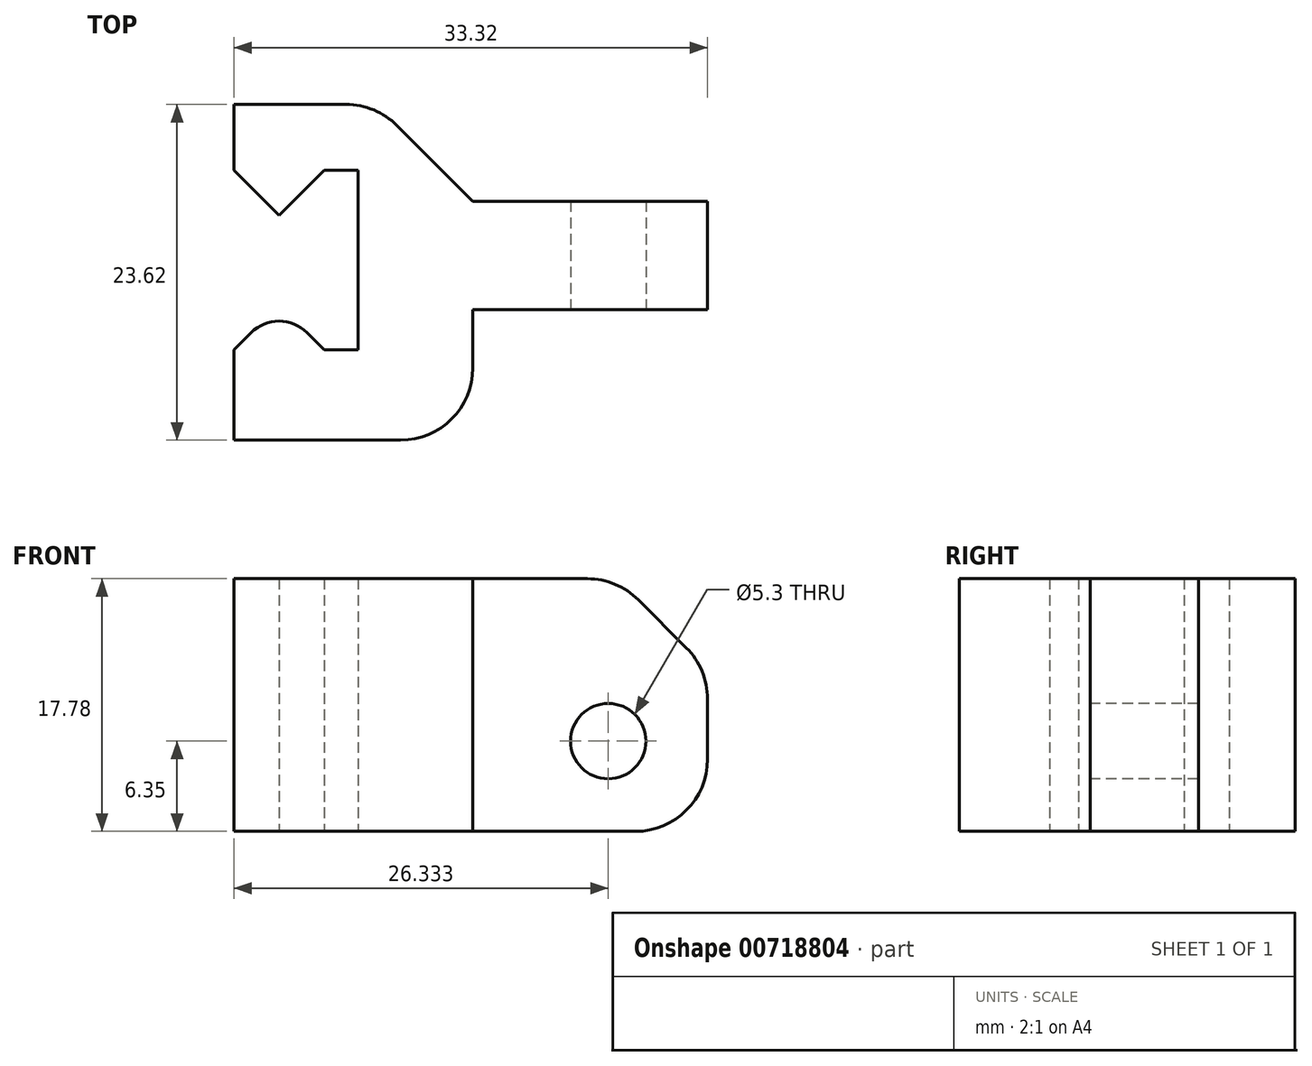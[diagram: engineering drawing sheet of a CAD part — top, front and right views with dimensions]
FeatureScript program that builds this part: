
annotation { "Feature Type Name" : "Feature", "Feature Type Description" : "" }
export const myFeature = defineFeature(function(context is Context, id is Id, definition is map)
    precondition{}
    {
        {
            var Q0;
            Q0=qCreatedBy(makeId("Top.planeOp"),FACE);
            var sketch = newSketch(context, id + "F0", { "sketchPlane" : qUnion([Q0])});
            skLineSegment(sketch, "E0", {"start": v(5.56, -11.6) * mm, "end": v(3.18, -11.6) * mm});
            skLineSegment(sketch, "E1", {"start": v(3.18, -11.6) * mm, "end": v(0, -8.43) * mm});
            skLineSegment(sketch, "E2", {"start": v(0, -8.43) * mm, "end": v(-3.18, -11.6) * mm});
            skLineSegment(sketch, "E3", {"start": v(-3.18, -11.6) * mm, "end": v(-3.18, -17.96) * mm});
            skLineSegment(sketch, "E4", {"start": v(-3.18, -17.96) * mm, "end": v(30.44, -17.96) * mm});
            skLineSegment(sketch, "E5", {"start": v(-0.4, 5.66) * mm, "end": v(6.81, 5.66) * mm});
            skLineSegment(sketch, "E6", {"start": v(6.81, 5.66) * mm, "end": v(30.44, -17.96) * mm});
            skPoint(sketch, "E7.endSnap0", {"position": v(13.63, -17.96) * mm});
            skLineSegment(sketch, "E8", {"start": v(13.63, -1.15) * mm, "end": v(13.63, -17.96) * mm});
            skLineSegment(sketch, "E9", {"start": v(5.56, -11.6) * mm, "end": v(5.56, 1.03) * mm});
            skLineSegment(sketch, "E10", {"start": v(3.18, 1.03) * mm, "end": v(5.56, 1.03) * mm});
            skLineSegment(sketch, "E11", {"start": v(3.18, 1.03) * mm, "end": v(0, -2.15) * mm});
            skLineSegment(sketch, "E12", {"start": v(0, -2.15) * mm, "end": v(-3.18, 1.03) * mm});
            skLineSegment(sketch, "E13", {"start": v(-3.18, 5.66) * mm, "end": v(-0.4, 5.66) * mm});
            skLineSegment(sketch, "E14", {"start": v(-3.18, 5.66) * mm, "end": v(-3.18, 1.03) * mm});
            skSolve(sketch);
        }
        {
            var Q0;
            Q0=makeQuery(id+"F0.imprint","IMPRINT",FACE,{"disambiguationData":[TD([[makeQuery(id+"F0.imprint","IMPRINT",EDGE,{"derivedFrom":sQuery(id+"F0.wireOp",EDGE,"ketpRVbD-6SFL-thPw-nqCE-cJDCLMVs4f7w")}),-1.0]])]});
            var Q1;
            Q1=makeQuery(id+"F0.imprint","IMPRINT",FACE,{"disambiguationData":[TD([[makeQuery(id+"F0.imprint","IMPRINT",EDGE,{"derivedFrom":sQuery(id+"F0.wireOp",EDGE,"E0")}),1.0]])]});
            extrude(context, id + "F1", {"entities" : qUnion([Q0, Q1]), "depth" : 17.78 * mm, "offsetDistance" : 25.4 * mm});
        }
        {
            var Q0;
            Q0=makeQuery(id+"F1.opExtrude","SWEPT_FACE",FACE,{"disambiguationData":[OSD([sQuery(id+"F0.wireOp",EDGE,"E8")])]});
            var sketch = newSketch(context, id + "F2", { "sketchPlane" : qUnion([Q0])});
            skLineSegment(sketch, "E15", {"start": v(-1.15, 0) * mm, "end": v(-1.15, 17.78) * mm});
            skLineSegment(sketch, "E16", {"start": v(-1.15, 17.78) * mm, "end": v(-8.77, 17.78) * mm});
            skLineSegment(sketch, "E17", {"start": v(-8.77, 17.78) * mm, "end": v(-8.77, 0) * mm});
            skLineSegment(sketch, "E18", {"start": v(-8.77, 0) * mm, "end": v(-1.15, 0) * mm});
            skSolve(sketch);
        }
        {
            var Q0;
            Q0 = qSketchRegion(id + "F2", true);
            extrude(context, id + "F3", {"entities" : qUnion([Q0]), "operationType" : NewBodyOperationType.ADD, "depth" : 16.5 * mm, "offsetDistance" : 25.4 * mm});
        }
        {
            var Q0;
            Q0=makeQuery(id+"F3.opExtrude","CAP_EDGE",EDGE,{"disambiguationData":[OSD([sQuery(id+"F2.wireOp",EDGE,"iHOXsHoF-hqfp-rUCR-3NdC-NWc7uM61uAc2")])],"isStart":false});
            var Q1;
            Q1=makeQuery(id+"F3.opExtrude","CAP_EDGE",EDGE,{"disambiguationData":[OSD([sQuery(id+"F2.wireOp",EDGE,"E16")])],"isStart":false});
            chamfer(context, id + "F4", {"entities" : qUnion([Q0, Q1]), "width" : 6.35 * mm, "tangentPropagation" : true});
        }
        {
            var Q0;
            Q0=makeQuery(id+"F3.opExtrude","SWEPT_FACE",FACE,{"disambiguationData":[OSD([sQuery(id+"F2.wireOp",EDGE,"E17")])]});
            var sketch = newSketch(context, id + "F5", { "sketchPlane" : qUnion([Q0])});
            skCircle(sketch, "E19", {"center": v(23.15, 6.35) * mm, "radius": 2.65 * mm});
            skSolve(sketch);
        }
        {
            var Q0;
            Q0 = qSketchRegion(id + "F5", true);
            extrude(context, id + "F6", {"entities" : qUnion([Q0]), "operationType" : NewBodyOperationType.REMOVE, "oppositeDirection" : true, "depth" : 25.4 * mm, "offsetDistance" : 25.4 * mm});
        }
        {
            var Q0;
            Q0=makeQuery(id+"F1.opExtrude","SWEPT_EDGE",EDGE,{"disambiguationData":[OSD([sQuery(id+"F0.wireOp",EDGE,"E1"),sQuery(id+"F0.wireOp",EDGE,"E2")])]});
            fillet(context, id + "F7", {"entities" : qUnion([Q0]), "radius" : 2.8 * mm, "tangentPropagation" : true, "allowEdgeOverflow" : false});
        }
        {
            var Q0;
            Q0=makeQuery(id+"F1.opExtrude","SWEPT_EDGE",EDGE,{"disambiguationData":[OSD([sQuery(id+"F0.wireOp",EDGE,"E5"),sQuery(id+"F0.wireOp",EDGE,"E6")])]});
            fillet(context, id + "F8", {"entities" : qUnion([Q0]), "radius" : 5.08 * mm, "tangentPropagation" : true, "allowEdgeOverflow" : false});
        }
        {
            var Q0;
            Q0=makeQuery(id+"F3.opExtrude","CAP_EDGE",EDGE,{"disambiguationData":[OSD([sQuery(id+"F2.wireOp",EDGE,"E18")])],"isStart":false});
            fillet(context, id + "F9", {"entities" : qUnion([Q0]), "radius" : 5.08 * mm, "tangentPropagation" : true, "allowEdgeOverflow" : false});
        }
        {
            var Q0;
            Q0=makeQuery(id+"F1.opExtrude","SWEPT_EDGE",EDGE,{"disambiguationData":[OSD([sQuery(id+"F0.wireOp",EDGE,"E4"),sQuery(id+"F0.wireOp",EDGE,"E8")])]});
            fillet(context, id + "F10", {"entities" : qUnion([Q0]), "radius" : 5.08 * mm, "tangentPropagation" : true, "allowEdgeOverflow" : false});
        }
        {
            var Q0;
            {var subQ0=sQuery(id+"F2.wireOp",EDGE,"E16");Q0=makeQuery(id+"F4.opChamfer","BLEND_EDGE",EDGE,{"blendedFrom":[makeQuery(id+"F3.opExtrude","CAP_EDGE",EDGE,{"disambiguationData":[OSD([subQ0])],"isStart":false}),makeQuery(id+"F3.opExtrude","CAP_FACE",FACE,{"disambiguationData":[OSD([sQuery(id+"F2.wireOp",EDGE,"E15"),subQ0,sQuery(id+"F2.wireOp",EDGE,"E17"),sQuery(id+"F2.wireOp",EDGE,"E18")])],"isStart":false})],"blendedInto":[makeQuery(id+"F3.opExtrude","CAP_FACE",FACE,{"disambiguationData":[OSD([sQuery(id+"F2.wireOp",EDGE,"E15"),subQ0,sQuery(id+"F2.wireOp",EDGE,"E17"),sQuery(id+"F2.wireOp",EDGE,"E18")])],"isStart":false})]});}
            var Q1;
            {var subQ0=sQuery(id+"F2.wireOp",EDGE,"E16");Q1=makeQuery(id+"F4.opChamfer","BLEND_EDGE",EDGE,{"blendedFrom":[makeQuery(id+"F3.opExtrude","CAP_EDGE",EDGE,{"disambiguationData":[OSD([subQ0])],"isStart":false}),makeQuery(id+"F3.boolean.opBoolean","MERGE",FACE,{"derivedFrom":[makeQuery(id+"F1.opExtrude","CAP_FACE",FACE,{"disambiguationData":[OSD([sQuery(id+"F0.wireOp",EDGE,"E0"),sQuery(id+"F0.wireOp",EDGE,"E1"),sQuery(id+"F0.wireOp",EDGE,"E2"),sQuery(id+"F0.wireOp",EDGE,"E3"),sQuery(id+"F0.wireOp",EDGE,"E4"),sQuery(id+"F0.wireOp",EDGE,"E5"),sQuery(id+"F0.wireOp",EDGE,"E6"),sQuery(id+"F0.wireOp",EDGE,"E8"),sQuery(id+"F0.wireOp",EDGE,"E9"),sQuery(id+"F0.wireOp",EDGE,"E10"),sQuery(id+"F0.wireOp",EDGE,"E11"),sQuery(id+"F0.wireOp",EDGE,"E12"),sQuery(id+"F0.wireOp",EDGE,"E13"),sQuery(id+"F0.wireOp",EDGE,"E14")])],"isStart":false}),makeQuery(id+"F3.opExtrude","SWEPT_FACE",FACE,{"disambiguationData":[OSD([subQ0])]})]})],"blendedInto":[makeQuery(id+"F3.boolean.opBoolean","MERGE",FACE,{"derivedFrom":[makeQuery(id+"F1.opExtrude","CAP_FACE",FACE,{"disambiguationData":[OSD([sQuery(id+"F0.wireOp",EDGE,"E0"),sQuery(id+"F0.wireOp",EDGE,"E1"),sQuery(id+"F0.wireOp",EDGE,"E2"),sQuery(id+"F0.wireOp",EDGE,"E3"),sQuery(id+"F0.wireOp",EDGE,"E4"),sQuery(id+"F0.wireOp",EDGE,"E5"),sQuery(id+"F0.wireOp",EDGE,"E6"),sQuery(id+"F0.wireOp",EDGE,"E8"),sQuery(id+"F0.wireOp",EDGE,"E9"),sQuery(id+"F0.wireOp",EDGE,"E10"),sQuery(id+"F0.wireOp",EDGE,"E11"),sQuery(id+"F0.wireOp",EDGE,"E12"),sQuery(id+"F0.wireOp",EDGE,"E13"),sQuery(id+"F0.wireOp",EDGE,"E14")])],"isStart":false}),makeQuery(id+"F3.opExtrude","SWEPT_FACE",FACE,{"disambiguationData":[OSD([subQ0])]})]})]});}
            fillet(context, id + "F11", {"entities" : qUnion([Q0, Q1]), "radius" : 5.08 * mm, "tangentPropagation" : true, "allowEdgeOverflow" : false});
        }
    });
